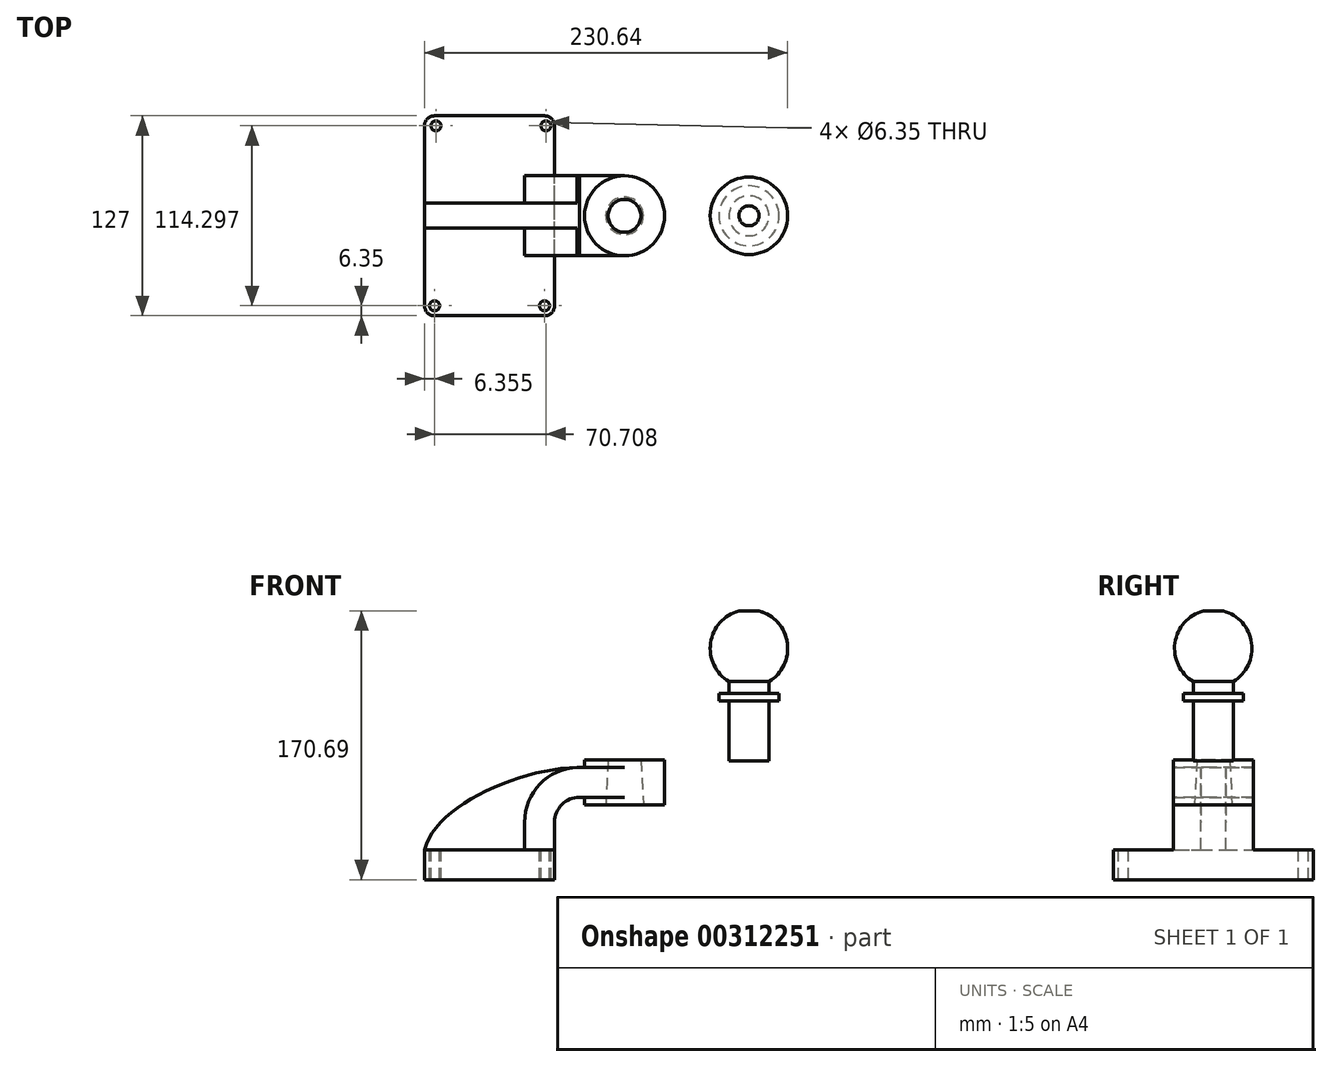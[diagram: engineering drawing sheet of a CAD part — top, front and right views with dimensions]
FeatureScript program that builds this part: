
annotation { "Feature Type Name" : "Feature", "Feature Type Description" : "" }
export const myFeature = defineFeature(function(context is Context, id is Id, definition is map)
    precondition{}
    {
        {
            var Q0;
            Q0=qCreatedBy(makeId("Front.planeOp"),FACE);
            var sketch = newSketch(context, id + "F0", { "sketchPlane" : qUnion([Q0])});
            skLineSegment(sketch, "E0.bottom", {"start": v(41.28, -8.48) * mm, "end": v(-41.28, -8.48) * mm});
            skLineSegment(sketch, "E0.top", {"start": v(41.28, 10.57) * mm, "end": v(-41.28, 10.57) * mm});
            skLineSegment(sketch, "E0.left", {"start": v(41.28, -8.48) * mm, "end": v(41.28, 10.57) * mm});
            skLineSegment(sketch, "E0.right", {"start": v(-41.28, -8.48) * mm, "end": v(-41.28, 10.57) * mm});
            skPoint(sketch, "E0.middle", {"position": v(0, 1.04) * mm});
            skLineSegment(sketch, "E1.bottom", {"start": v(60.33, 39.14) * mm, "end": v(111.12, 39.14) * mm});
            skLineSegment(sketch, "E1.top", {"start": v(60.32, 67.72) * mm, "end": v(111.12, 67.72) * mm});
            skLineSegment(sketch, "E1.left", {"start": v(60.33, 39.14) * mm, "end": v(60.32, 67.72) * mm});
            skLineSegment(sketch, "E1.right", {"start": v(111.12, 39.14) * mm, "end": v(111.12, 67.72) * mm});
            skPoint(sketch, "E1.middle", {"position": v(85.73, 53.43) * mm});
            skLineSegment(sketch, "E2", {"start": v(41.27, 10.57) * mm, "end": v(41.27, 28.04) * mm});
            skArc(sketch, "E3", {"start": v(41.27, 28.04) * mm, "mid": v(45.92, 39.27) * mm, "end": v(57.15, 43.92) * mm});
            skLineSegment(sketch, "E4", {"start": v(57.15, 43.92) * mm, "end": v(85.73, 43.92) * mm});
            skLineSegment(sketch, "E5.0", {"start": v(57.15, 62.97) * mm, "end": v(85.72, 62.97) * mm});
            skArc(sketch, "E5.1", {"start": v(22.23, 28.04) * mm, "mid": v(32.45, 52.74) * mm, "end": v(57.15, 62.97) * mm});
            skLineSegment(sketch, "E5.2", {"start": v(22.23, 10.57) * mm, "end": v(22.23, 28.04) * mm});
            skLineSegment(sketch, "E6", {"start": v(85.72, 39.14) * mm, "end": v(85.72, 67.72) * mm});
            skFitSpline(sketch, "E7", {"points": [v(-41.28, 10.57) * mm, v(57.15, 62.97) * mm], "startDerivative": vector(19.67, 84.26) * mm, "endDerivative": vector(113.6, 1.52) * mm});
            skSolve(sketch);
        }
        {
            var Q0;
            Q0=makeQuery(id+"F0.imprint","IMPRINT",FACE,{"disambiguationData":[TD([[makeQuery(id+"F0.imprint","IMPRINT",EDGE,{"derivedFrom":sQuery(id+"F0.wireOp",EDGE,"E0.bottom")}),-1.0]])]});
            extrude(context, id + "F1", {"entities" : qUnion([Q0]), "endBound" : BoundingType.SYMMETRIC, "depth" : 127 * mm});
        }
        {
            var Q0;
            {var subQ1=sQuery(id+"F0.wireOp",EDGE,"E2");Q0=makeQuery(id+"F0.imprint","IMPRINT",FACE,{"disambiguationData":[TD([[makeQuery(id+"F0.imprint","IMPRINT",EDGE,{"derivedFrom":subQ1}),1.0]])]});}
            var Q1;
            {var subQ0=sQuery(id+"F0.wireOp",EDGE,"E4");var subQ1=sQuery(id+"F0.wireOp",EDGE,"E1.left");var subQ2=makeQuery(id+"F0.imprint","INTERSECT",VERTEX,{"derivedFrom":[subQ1,subQ0]});Q1=makeQuery(id+"F0.imprint","IMPRINT",FACE,{"disambiguationData":[TD([[makeQuery(id+"F0.imprint","IMPRINT",EDGE,{"disambiguationData":[TD([[subQ2,-1.0]])],"derivedFrom":subQ1}),-1.0]])]});}
            extrude(context, id + "F2", {"entities" : qUnion([Q0, Q1]), "operationType" : NewBodyOperationType.ADD, "endBound" : BoundingType.SYMMETRIC, "depth" : 50.8 * mm});
        }
        {
            var Q0;
            {var subQ3=sQuery(id+"F0.wireOp",EDGE,"E5.2");Q0=makeQuery(id+"F0.imprint","IMPRINT",FACE,{"disambiguationData":[TD([[makeQuery(id+"F0.imprint","IMPRINT",EDGE,{"derivedFrom":subQ3}),1.0]])]});}
            extrude(context, id + "F3", {"entities" : qUnion([Q0]), "operationType" : NewBodyOperationType.ADD, "endBound" : BoundingType.SYMMETRIC, "depth" : 15.88 * mm});
        }
        {
            var Q0;
            {var subQ4=sQuery(id+"F0.wireOp",EDGE,"E1.right");Q0=makeQuery(id+"F0.imprint","IMPRINT",FACE,{"disambiguationData":[TD([[makeQuery(id+"F0.imprint","IMPRINT",EDGE,{"derivedFrom":subQ4}),1.0]])]});}
            var Q1;
            Q1=sQuery(id+"F0.wireOp",EDGE,"E6");
            revolve(context, id + "F4", {"operationType" : NewBodyOperationType.ADD, "entities" : qUnion([Q0]), "axis" : qUnion([Q1]), "revolveType" : RevolveType.FULL});
        }
        {
            var Q0;
            Q0=makeQuery(id+"F1.opExtrude","CAP_EDGE",EDGE,{"disambiguationData":[OSD([sQuery(id+"F0.wireOp",EDGE,"E0.right")])],"isStart":false});
            var Q1;
            Q1=makeQuery(id+"F1.opExtrude","CAP_EDGE",EDGE,{"disambiguationData":[OSD([sQuery(id+"F0.wireOp",EDGE,"E0.left")])],"isStart":false});
            var Q2;
            Q2=makeQuery(id+"F1.opExtrude","CAP_EDGE",EDGE,{"disambiguationData":[OSD([sQuery(id+"F0.wireOp",EDGE,"E0.left")])],"isStart":true});
            var Q3;
            Q3=makeQuery(id+"F1.opExtrude","CAP_EDGE",EDGE,{"disambiguationData":[OSD([sQuery(id+"F0.wireOp",EDGE,"E0.right")])],"isStart":true});
            fillet(context, id + "F5", {"entities" : qUnion([Q0, Q1, Q2, Q3]), "radius" : 6.35 * mm, "tangentPropagation" : true, "allowEdgeOverflow" : false});
        }
        {
            var Q0;
            Q0=makeQuery(id+"F4.opRevolve","SWEPT_FACE",FACE,{"disambiguationData":[OSD([sQuery(id+"F0.wireOp",EDGE,"E1.top")])]});
            var sketch = newSketch(context, id + "F6", { "sketchPlane" : qUnion([Q0])});
            skCircle(sketch, "E8", {"center": v(85.72, 0) * mm, "radius": 10.43 * mm});
            skSolve(sketch);
        }
        {
            var Q0;
            Q0 = qSketchRegion(id + "F6", true);
            extrude(context, id + "F7", {"entities" : qUnion([Q0]), "operationType" : NewBodyOperationType.REMOVE, "endBound" : BoundingType.THROUGH_ALL, "oppositeDirection" : true, "depth" : 25.4 * mm, "hasDraft" : true, "draftAngle" : 3 * degree});
        }
        {
            var Q0;
            {var subQ4=sQuery(id+"F0.wireOp",EDGE,"E0.top");var subQ5=sQuery(id+"F0.wireOp",EDGE,"E0.right");var subQ6=sQuery(id+"F0.wireOp",EDGE,"E0.left");Q0=makeQuery(id+"F3.boolean.opBoolean","SPLIT",FACE,{"disambiguationData":[TD([makeQuery(id+"F1.opExtrude","CAP_FACE",FACE,{"disambiguationData":[OSD([sQuery(id+"F0.wireOp",EDGE,"E0.bottom"),subQ4,subQ6,subQ5])],"isStart":false})])],"derivedFrom":makeQuery(id+"F1.opExtrude","SWEPT_FACE",FACE,{"disambiguationData":[OSD([subQ4])]})});}
            var sketch = newSketch(context, id + "F8", { "sketchPlane" : qUnion([Q0])});
            skCircle(sketch, "E9", {"center": v(-34.93, -57.15) * mm, "radius": 3.17 * mm});
            skCircle(sketch, "E10.0.1.0", {"center": v(-34.07, 57.15) * mm, "radius": 3.17 * mm});
            skCircle(sketch, "E10.1.0.0", {"center": v(34.92, -57.15) * mm, "radius": 3.17 * mm});
            skCircle(sketch, "E10.1.1.0", {"center": v(35.78, 57.15) * mm, "radius": 3.17 * mm});
            skLineSegment(sketch, "E10.direction1", {"start": v(-34.93, -57.15) * mm, "end": v(34.92, -57.15) * mm, "construction": true});
            skLineSegment(sketch, "E10.direction2", {"start": v(-34.92, -57.15) * mm, "end": v(-34.07, 57.15) * mm, "construction": true});
            skSolve(sketch);
        }
        {
            var Q0;
            Q0=sQuery(id+"F8.wireOp",VERTEX,"E10.1.0.0.center");
            var Q1;
            Q1=sQuery(id+"F8.wireOp",VERTEX,"E9.center");
            var Q2;
            Q2=sQuery(id+"F8.wireOp",VERTEX,"E10.1.1.0.center");
            var Q3;
            Q3=sQuery(id+"F8.wireOp",VERTEX,"E10.0.1.0.center");
            var Q4;
            Q4=makeQuery(id+"F1.opExtrude","SWEPT_BODY",BODY,{"disambiguationData":[OSD([sQuery(id+"F0.wireOp",EDGE,"E0.bottom"),sQuery(id+"F0.wireOp",EDGE,"E0.top"),sQuery(id+"F0.wireOp",EDGE,"E0.left"),sQuery(id+"F0.wireOp",EDGE,"E0.right")])]});
            hole(context, id + "F9", {"style" : HoleStyle.SIMPLE, "endStyle" : HoleEndStyle.THROUGH, "holeDiameter" : 6.35 * mm, "tappedDepth" : 12.7 * mm, "tapClearance" : 3, "locations" : qUnion([Q0, Q1, Q2, Q3]), "scope" : qUnion([Q4])});
        }
        {
            var Q0;
            Q0=qCreatedBy(makeId("Front.planeOp"),FACE);
            var sketch = newSketch(context, id + "F10", { "sketchPlane" : qUnion([Q0])});
            skLineSegment(sketch, "E11", {"start": v(164.76, 66.96) * mm, "end": v(177.46, 66.96) * mm});
            skLineSegment(sketch, "E12", {"start": v(177.46, 66.96) * mm, "end": v(177.46, 105.06) * mm});
            skLineSegment(sketch, "E13", {"start": v(177.46, 105.06) * mm, "end": v(183.8, 105.06) * mm});
            skLineSegment(sketch, "E14", {"start": v(183.8, 105.06) * mm, "end": v(183.8, 109.82) * mm});
            skLineSegment(sketch, "E15", {"start": v(183.8, 109.82) * mm, "end": v(177.46, 109.82) * mm});
            skArc(sketch, "E16", {"start": v(177.46, 117.36) * mm, "mid": v(189.12, 141.89) * mm, "end": v(171.1, 162.21) * mm});
            skLineSegment(sketch, "E17", {"start": v(177.46, 109.82) * mm, "end": v(177.46, 117.36) * mm});
            skLineSegment(sketch, "E18", {"start": v(164.76, 162.21) * mm, "end": v(171.1, 162.21) * mm});
            skLineSegment(sketch, "E19", {"start": v(164.76, 162.21) * mm, "end": v(164.76, 66.96) * mm});
            skSolve(sketch);
        }
        {
            var Q0;
            Q0 = qSketchRegion(id + "F10", true);
            var Q1;
            Q1=sQuery(id+"F10.wireOp",EDGE,"E19");
            revolve(context, id + "F11", {"entities" : qUnion([Q0]), "axis" : qUnion([Q1]), "revolveType" : RevolveType.FULL});
        }
    });
